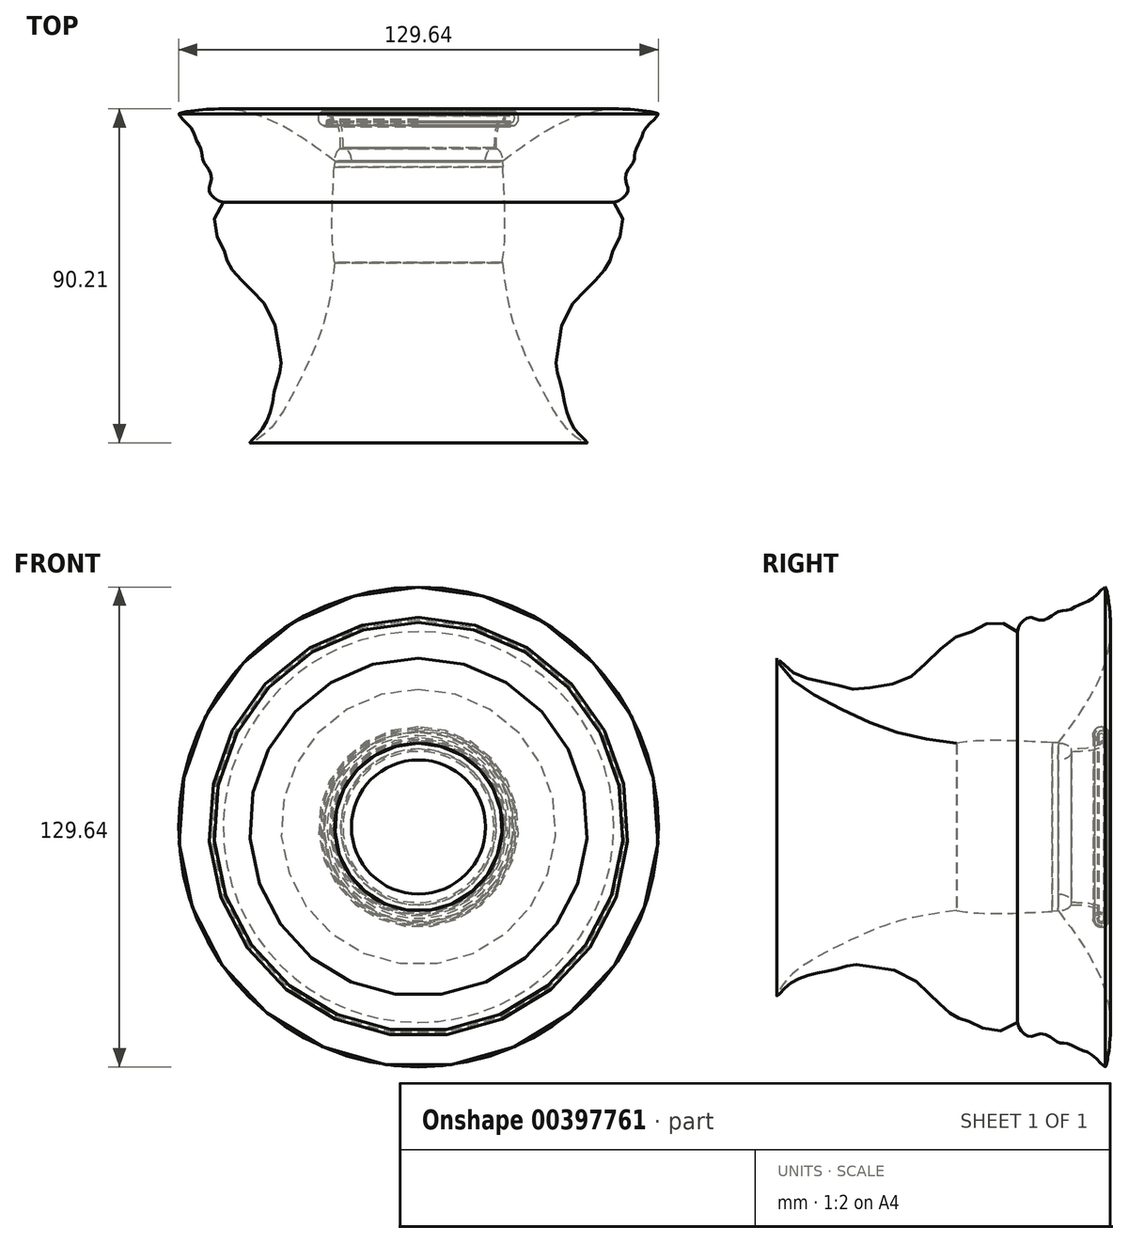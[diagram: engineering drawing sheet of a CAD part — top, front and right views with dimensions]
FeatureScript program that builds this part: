
annotation { "Feature Type Name" : "Feature", "Feature Type Description" : "" }
export const myFeature = defineFeature(function(context is Context, id is Id, definition is map)
    precondition{}
    {
        {
            var Q0;
            Q0=qCreatedBy(makeId("Top.planeOp"),FACE);
            var sketch = newSketch(context, id + "F0", { "sketchPlane" : qUnion([Q0])});
            skEllipticalArc(sketch, "E0", {});
            skEllipticalArc(sketch, "E1", {});
            skFitSpline(sketch, "E2", {"points": [v(2.3, 20.9) * mm, v(2.89, 0) * mm, v(1.74, -9.47) * mm], "startDerivative": vector(2.01, -38.53) * mm, "endDerivative": vector(-3.6, -21.18) * mm});
            skFitSpline(sketch, "E3", {"points": [v(-2.3, 20.9) * mm, v(-3.05, 0) * mm, v(-1.74, -9.47) * mm], "startDerivative": vector(-2.5, -38.54) * mm, "endDerivative": vector(4.14, -21.16) * mm});
            skEllipticalArc(sketch, "E4", {});
            skFitSpline(sketch, "E5", {"points": [v(-2.3, 20.9) * mm, v(0, 20.9) * mm, v(2.3, 20.9) * mm], "startDerivative": vector(4.7, -2.5) * mm, "endDerivative": vector(4.7, 2.5) * mm});
            skFitSpline(sketch, "E6", {"points": [v(-2.4, 19.25) * mm, v(0, 18.83) * mm, v(2.38, 19.24) * mm], "startDerivative": vector(4.9, -2.33) * mm, "endDerivative": vector(4.87, 2.3) * mm});
            skFitSpline(sketch, "E7", {"points": [v(2.3, 20.9) * mm, v(15.85, 30.1) * mm, v(32.92, 34.98) * mm, v(44.41, 33.58) * mm, v(36.58, 33.58) * mm, v(28.57, 33.06) * mm, v(16.1, 28.61) * mm, v(2.38, 19.24) * mm], "startDerivative": vector(81.12, 61.53) * mm, "endDerivative": vector(-77.6, -62.7) * mm});
            skFitSpline(sketch, "E8", {"points": [v(2.38, 19.24) * mm, v(12.47, 14.95) * mm, v(28.81, 10.34) * mm, v(32.38, 9.81) * mm, v(34.78, 10.9) * mm, v(36.24, 13.24) * mm, v(35.51, 15.87) * mm, v(36.39, 18.85) * mm, v(37.78, 20.9) * mm, v(38.21, 23.65) * mm, v(39.54, 26.37) * mm, v(41.1, 29.93) * mm, v(44.41, 33.58) * mm], "startDerivative": vector(70.32, -29.03) * mm, "endDerivative": vector(18.2, 40.24) * mm});
            skFitSpline(sketch, "E9", {"points": [v(2.22, -6.62) * mm, v(4.74, -21.24) * mm, v(9.72, -34.27) * mm, v(16.75, -47.59) * mm, v(22.16, -53.59) * mm, v(25.24, -55.2) * mm, v(22.5, -52.37) * mm, v(20.7, -49.53) * mm, v(19.34, -45.75) * mm, v(18.72, -42.23) * mm, v(17.47, -37.47) * mm, v(16.77, -34.04) * mm, v(17.42, -29.11) * mm, v(19.07, -20.9) * mm, v(22.35, -16.46) * mm, v(27.45, -11.2) * mm, v(31.06, -6.62) * mm, v(32.38, -2.5) * mm, v(34.51, 1.61) * mm, v(34.51, 6.21) * mm, v(32.38, 9.81) * mm], "startDerivative": vector(24.83, -191.18) * mm, "endDerivative": vector(-60.54, 80.48) * mm});
            skEllipse(sketch, "E10", {"center": v(28.24, 24.96) * mm, "majorRadius": 3.27 * mm, "minorRadius": 1.36 * mm, "majorAxis": v(0.84, 0.54)});
            skEllipse(sketch, "E11", {"center": v(28.24, 24.96) * mm, "majorRadius": 1.8 * mm, "minorRadius": 0.84 * mm, "majorAxis": v(0.82, 0.57)});
            skEllipse(sketch, "E12", {"center": v(24.15, 5.65) * mm, "majorRadius": 2.9 * mm, "minorRadius": 1.52 * mm, "majorAxis": v(0.82, -0.57)});
            skEllipse(sketch, "E13", {"center": v(24.15, 5.65) * mm, "majorRadius": 2.05 * mm, "minorRadius": 0.86 * mm, "majorAxis": v(0.76, -0.65)});
            skFitSpline(sketch, "E14", {"points": [v(2.22, -6.62) * mm, v(2.22, -6.56) * mm], "startDerivative": vector(0, 0.06) * mm, "endDerivative": vector(0, 0.06) * mm});
            skLineSegment(sketch, "E15", {"start": v(2.22, -6.56) * mm, "end": v(2.22, -6.55) * mm});
            skArc(sketch, "E16", {"start": v(3.2, 30.63) * mm, "mid": v(6.58, 31.93) * mm, "end": v(4.26, 34.7) * mm});
            skFitSpline(sketch, "E17", {"points": [v(0, 24.44) * mm, v(0.17, 27.52) * mm, v(0.46, 30.02) * mm, v(1.38, 32.67) * mm, v(2.86, 34.16) * mm, v(4.26, 34.7) * mm, v(5.9, 34.15) * mm, v(6.54, 33.17) * mm, v(6.42, 31.5) * mm, v(5.17, 30.4) * mm, v(3.2, 30.63) * mm, v(2.58, 32.37) * mm, v(3.43, 33.46) * mm, v(4.47, 33.63) * mm, v(5.32, 33.33) * mm, v(5.54, 32.83) * mm, v(5.46, 31.98) * mm, v(5, 31.43) * mm, v(4.06, 31.54) * mm, v(3.73, 32.07) * mm, v(4.64, 31.8) * mm, v(5.1, 32.7) * mm, v(4.5, 33.16) * mm, v(3.6, 33) * mm, v(3.02, 32.23) * mm, v(3.46, 31.08) * mm, v(5.02, 30.75) * mm, v(6.02, 31.63) * mm, v(6.13, 33.11) * mm, v(5.5, 33.9) * mm, v(4.27, 34.21) * mm, v(3.05, 33.74) * mm, v(1.87, 32.34) * mm, v(1.14, 29.93) * mm, v(0.72, 27.44) * mm, v(0.67, 24.28) * mm], "startDerivative": vector(3.76, 75.56) * mm, "endDerivative": vector(0.96, -77.04) * mm});
            skFitSpline(sketch, "E18", {"points": [v(2.38, 19.24) * mm, v(6.91, 21.58) * mm, v(16.42, 27.5) * mm, v(28.7, 31.98) * mm, v(36.58, 32.61) * mm, v(43.66, 33.11) * mm, v(36.58, 31.98) * mm, v(28.73, 31.35) * mm, v(16.53, 26.57) * mm, v(7.08, 21.11) * mm, v(2.38, 19.24) * mm]});
            skFitSpline(sketch, "E19", {"points": [v(3.89, 16) * mm, v(8, 13.7) * mm, v(12.47, 11.56) * mm, v(16.7, 10.04) * mm, v(24.01, 8.77) * mm, v(20.07, 8.11) * mm, v(20.15, 5.49) * mm, v(23.1, 2.28) * mm, v(26.97, 1.63) * mm, v(29.1, 2.7) * mm, v(27.05, 0.15) * mm, v(22.12, 1.05) * mm, v(18.5, 4.91) * mm, v(17.52, 7.43) * mm, v(12.47, 9.76) * mm, v(7.59, 12.3) * mm, v(3.89, 16) * mm]});
            skFitSpline(sketch, "E20", {"points": [v(5.46, 9.78) * mm, v(10.98, 6.1) * mm, v(15.51, 2.9) * mm, v(19.7, -3.33) * mm, v(18.04, -7.97) * mm, v(12.47, -7.2) * mm, v(12.47, -2.77) * mm, v(15.68, -3.9) * mm, v(13.83, -5.32) * mm, v(17.46, -5.96) * mm, v(17.35, -3.33) * mm, v(14.6, 0) * mm, v(9.86, 0) * mm, v(8.99, -8.85) * mm, v(10.9, -14.68) * mm, v(14.72, -14.4) * mm, v(16.47, -12.87) * mm, v(12.47, -19.72) * mm, v(12.04, -24.36) * mm, v(10.55, -27.84) * mm, v(8.92, -21.48) * mm, v(8.26, -16.46) * mm, v(7.13, -8.6) * mm, v(6.38, 0) * mm, v(6.08, 2.9) * mm, v(5.85, 7.32) * mm, v(5.46, 9.78) * mm]});
            skPoint(sketch, "E21.6.internal.snap0", {"position": v(27.52, 26.1) * mm});
            skFitSpline(sketch, "E21", {"points": [v(7.6, 19.77) * mm, v(15.95, 23.96) * mm, v(21.25, 26.36) * mm, v(24.34, 28.44) * mm, v(23.14, 24.47) * mm, v(23.41, 22.07) * mm, v(27.52, 21.38) * mm, v(29.13, 21.66) * mm, v(27.1, 19.54) * mm, v(23.04, 18.8) * mm, v(17.7, 18.9) * mm, v(12.3, 19.08) * mm, v(7.6, 19.77) * mm]});
            skFitSpline(sketch, "E22.MirrorCS", {"points": [v(-2.22, -6.62) * mm, v(-2.22, -6.56) * mm], "startDerivative": vector(0, 0.06) * mm, "endDerivative": vector(0, 0.06) * mm});
            skLineSegment(sketch, "E23.MirrorCS", {"start": v(-2.22, -6.56) * mm, "end": v(-2.22, -6.55) * mm});
            skEllipticalArc(sketch, "E24.MirrorCS", {});
            skEllipticalArc(sketch, "E25.MirrorCS", {});
            skFitSpline(sketch, "E26.MirrorCS", {"points": [v(2.3, 20.9) * mm, v(0, 20.9) * mm, v(-2.3, 20.9) * mm], "startDerivative": vector(-4.7, -2.5) * mm, "endDerivative": vector(-4.7, 2.5) * mm});
            skFitSpline(sketch, "E27.MirrorCS", {"points": [v(2.4, 19.25) * mm, v(0, 18.83) * mm, v(-2.38, 19.24) * mm], "startDerivative": vector(-4.9, -2.33) * mm, "endDerivative": vector(-4.87, 2.3) * mm});
            skEllipticalArc(sketch, "E28.MirrorCS", {});
            skLineSegment(sketch, "E29", {"start": v(-20.4, 52.86) * mm, "end": v(-20.4, -60.76) * mm});
            skPoint(sketch, "E30.orphan", {"position": v(0, 43.1) * mm});
            const initialGuessF0  = {"E0": [0, 0.02090463444890858, 0, -1, 0.0035310519394098046, 0.002297039903684678, 1.5707963267948966, 4.71238898038469], "E1": [0, -0.009469367382299913, 0, 1, 0.0035901373358472096, 0.001739675895624183, 1.5707963267948966, 4.71238898038469], "E4": [0.001387894892873516, 0.023718264862181527, 0.3162766123089874, -0.9486670145558718, 0.0018780809074936957, 0.0005518705882354958, 4.293777265012078, 0.42567047345905185], "E24.MirrorCS": [0, 0.02090463444890858, 0, -1, 0.0035310519394098046, 0.002297039903684678, 1.5707963267948966, 4.71238898038469], "E25.MirrorCS": [-0.001387894892873516, 0.023718264862181527, -0.3162766123089874, -0.9486670145558718, 0.0018780809074936957, 0.0005518705882354958, 5.8575148337205345, 1.9894080421675087], "E28.MirrorCS": [0, -0.009469367382299913, 0, 1, 0.0035901373358472096, 0.001739675895624183, 1.5707963267948966, 4.71238898038469]};
            skSetInitialGuess(sketch, initialGuessF0);
            skSolve(sketch);
        }
        {
            var Q0;
            Q0=makeQuery(id+"F0.imprint","IMPRINT",FACE,{"disambiguationData":[TD([[makeQuery(id+"F0.imprint","IMPRINT",EDGE,{"derivedFrom":sQuery(id+"F0.wireOp",EDGE,"E10")}),-1.0]])]});
            var Q1;
            Q1=makeQuery(id+"F0.imprint","IMPRINT",FACE,{"disambiguationData":[TD([[makeQuery(id+"F0.imprint","IMPRINT",EDGE,{"derivedFrom":sQuery(id+"F0.wireOp",EDGE,"E19")}),-1.0]])]});
            var Q2;
            Q2=makeQuery(id+"F0.imprint","IMPRINT",FACE,{"disambiguationData":[TD([[makeQuery(id+"F0.imprint","IMPRINT",EDGE,{"derivedFrom":sQuery(id+"F0.wireOp",EDGE,"E20")}),-1.0]])]});
            var Q3;
            Q3=makeQuery(id+"F0.imprint","IMPRINT",FACE,{"disambiguationData":[TD([[makeQuery(id+"F0.imprint","IMPRINT",EDGE,{"derivedFrom":sQuery(id+"F0.wireOp",EDGE,"E21")}),-1.0]])]});
            var Q4;
            {var subQ0=sQuery(id+"F0.wireOp",EDGE,"E9");Q4=makeQuery(id+"F0.imprint","IMPRINT",FACE,{"disambiguationData":[TD([[makeQuery(id+"F0.imprint","IMPRINT",EDGE,{"derivedFrom":subQ0}),1.0]])]});}
            var Q5;
            {var subQ1=sQuery(id+"F0.wireOp",EDGE,"E7");var subQ5=makeQuery(id+"F0.imprint","INTERSECT",VERTEX,{"derivedFrom":[subQ1,sQuery(id+"F0.wireOp",EDGE,"E8")]});Q5=makeQuery(id+"F0.imprint","IMPRINT",FACE,{"disambiguationData":[TD([[makeQuery(id+"F0.imprint","IMPRINT",EDGE,{"disambiguationData":[TD([[subQ5,-1.0]])],"derivedFrom":subQ1}),-1.0]])]});}
            var Q6;
            {var subQ0=sQuery(id+"F0.wireOp",EDGE,"E28.MirrorCS");Q6=makeQuery(id+"F0.imprint","IMPRINT",FACE,{"disambiguationData":[TD([[makeQuery(id+"F0.imprint","IMPRINT",EDGE,{"derivedFrom":subQ0}),1.0]])]});}
            var Q7;
            Q7=makeQuery(id+"F0.imprint","IMPRINT",FACE,{"disambiguationData":[TD([[makeQuery(id+"F0.imprint","IMPRINT",EDGE,{"derivedFrom":sQuery(id+"F0.wireOp",EDGE,"E10")}),1.0]])]});
            var Q8;
            Q8=makeQuery(id+"F0.imprint","IMPRINT",FACE,{"disambiguationData":[TD([[makeQuery(id+"F0.imprint","IMPRINT",EDGE,{"derivedFrom":sQuery(id+"F0.wireOp",EDGE,"E12")}),1.0]])]});
            var Q9;
            {var subQ0=sQuery(id+"F0.wireOp",EDGE,"E7");var subQ1=makeQuery(id+"F0.imprint","INTERSECT",VERTEX,{"derivedFrom":[subQ0,sQuery(id+"F0.wireOp",EDGE,"E27.MirrorCS")]});Q9=makeQuery(id+"F0.imprint","IMPRINT",FACE,{"disambiguationData":[TD([[makeQuery(id+"F0.imprint","IMPRINT",EDGE,{"disambiguationData":[TD([[subQ1,1.0]])],"derivedFrom":subQ0}),1.0]])]});}
            var Q10;
            {var subQ0=sQuery(id+"F0.wireOp",EDGE,"E17");var subQ1=sQuery(id+"F0.wireOp",EDGE,"E16");var subQ10=makeQuery(id+"F0.imprint","INTERSECT",VERTEX,{"disambiguationData":[OD(0.0)],"derivedFrom":[subQ1,subQ0]});Q10=makeQuery(id+"F0.imprint","IMPRINT",FACE,{"disambiguationData":[TD([[makeQuery(id+"F0.imprint","IMPRINT",EDGE,{"disambiguationData":[TD([[subQ10,-1.0]])],"derivedFrom":subQ1}),1.0]])]});}
            var Q11;
            Q11=makeQuery(id+"F0.imprint","IMPRINT",FACE,{"disambiguationData":[TD([[makeQuery(id+"F0.imprint","IMPRINT",EDGE,{"derivedFrom":sQuery(id+"F0.wireOp",EDGE,"E11")}),1.0]])]});
            var Q12;
            Q12=makeQuery(id+"F0.imprint","IMPRINT",FACE,{"disambiguationData":[TD([[makeQuery(id+"F0.imprint","IMPRINT",EDGE,{"derivedFrom":sQuery(id+"F0.wireOp",EDGE,"E13")}),1.0]])]});
            var Q13;
            {var subQ0=sQuery(id+"F0.wireOp",EDGE,"E4");Q13=makeQuery(id+"F0.imprint","IMPRINT",FACE,{"disambiguationData":[TD([[makeQuery(id+"F0.imprint","IMPRINT",EDGE,{"derivedFrom":subQ0}),1.0]])]});}
            var Q14;
            {var subQ0=sQuery(id+"F0.wireOp",EDGE,"E17");var subQ1=sQuery(id+"F0.wireOp",EDGE,"E16");var subQ2=makeQuery(id+"F0.imprint","INTERSECT",VERTEX,{"disambiguationData":[OD(3.0)],"derivedFrom":[subQ1,subQ0]});Q14=makeQuery(id+"F0.imprint","IMPRINT",FACE,{"disambiguationData":[TD([[makeQuery(id+"F0.imprint","IMPRINT",EDGE,{"disambiguationData":[TD([[subQ2,-1.0]])],"derivedFrom":subQ1}),-1.0]])]});}
            var Q15;
            {var subQ0=sQuery(id+"F0.wireOp",EDGE,"E17");var subQ1=sQuery(id+"F0.wireOp",EDGE,"E16");var subQ2=makeQuery(id+"F0.imprint","INTERSECT",VERTEX,{"disambiguationData":[OD(4.0)],"derivedFrom":[subQ1,subQ0]});Q15=makeQuery(id+"F0.imprint","IMPRINT",FACE,{"disambiguationData":[TD([[makeQuery(id+"F0.imprint","IMPRINT",EDGE,{"disambiguationData":[TD([[subQ2,-1.0]])],"derivedFrom":subQ1}),1.0]])]});}
            var Q16;
            {var subQ0=sQuery(id+"F0.wireOp",EDGE,"E17");var subQ1=sQuery(id+"F0.wireOp",EDGE,"E16");var subQ2=makeQuery(id+"F0.imprint","INTERSECT",VERTEX,{"disambiguationData":[OD(5.0)],"derivedFrom":[subQ1,subQ0]});Q16=makeQuery(id+"F0.imprint","IMPRINT",FACE,{"disambiguationData":[TD([[makeQuery(id+"F0.imprint","IMPRINT",EDGE,{"disambiguationData":[TD([[subQ2,-1.0]])],"derivedFrom":subQ1}),-1.0]])]});}
            var Q17;
            {var subQ0=sQuery(id+"F0.wireOp",EDGE,"E17");var subQ1=sQuery(id+"F0.wireOp",EDGE,"E16");var subQ2=makeQuery(id+"F0.imprint","INTERSECT",VERTEX,{"disambiguationData":[OD(0.0)],"derivedFrom":[subQ1,subQ0]});Q17=makeQuery(id+"F0.imprint","IMPRINT",FACE,{"disambiguationData":[TD([[makeQuery(id+"F0.imprint","IMPRINT",EDGE,{"disambiguationData":[TD([[subQ2,-1.0]])],"derivedFrom":subQ1}),-1.0]])]});}
            var Q18;
            {var subQ0=sQuery(id+"F0.wireOp",EDGE,"E17");var subQ1=sQuery(id+"F0.wireOp",EDGE,"E16");var subQ2=makeQuery(id+"F0.imprint","INTERSECT",VERTEX,{"disambiguationData":[OD(2.0)],"derivedFrom":[subQ1,subQ0]});Q18=makeQuery(id+"F0.imprint","IMPRINT",FACE,{"disambiguationData":[TD([[makeQuery(id+"F0.imprint","IMPRINT",EDGE,{"disambiguationData":[TD([[subQ2,-1.0]])],"derivedFrom":subQ1}),1.0]])]});}
            var Q19;
            {var subQ0=sQuery(id+"F0.wireOp",EDGE,"E17");var subQ1=sQuery(id+"F0.wireOp",EDGE,"E16");var subQ2=makeQuery(id+"F0.imprint","INTERSECT",VERTEX,{"disambiguationData":[OD(1.0)],"derivedFrom":[subQ1,subQ0]});Q19=makeQuery(id+"F0.imprint","IMPRINT",FACE,{"disambiguationData":[TD([[makeQuery(id+"F0.imprint","IMPRINT",EDGE,{"disambiguationData":[TD([[subQ2,1.0]])],"derivedFrom":subQ1}),1.0]])]});}
            var Q20;
            {var subQ5=sQuery(id+"F0.wireOp",EDGE,"E4");Q20=makeQuery(id+"F0.imprint","IMPRINT",FACE,{"disambiguationData":[TD([[makeQuery(id+"F0.imprint","IMPRINT",EDGE,{"derivedFrom":subQ5}),-1.0]])]});}
            var Q21;
            {var subQ0=sQuery(id+"F0.wireOp",EDGE,"E25.MirrorCS");Q21=makeQuery(id+"F0.imprint","IMPRINT",FACE,{"disambiguationData":[TD([[makeQuery(id+"F0.imprint","IMPRINT",EDGE,{"derivedFrom":subQ0}),1.0]])]});}
            var Q22;
            {var subQ0=sQuery(id+"F0.wireOp",EDGE,"E26.MirrorCS");Q22=makeQuery(id+"F0.imprint","IMPRINT",FACE,{"disambiguationData":[TD([[makeQuery(id+"F0.imprint","IMPRINT",EDGE,{"derivedFrom":subQ0}),1.0]])]});}
            var Q23;
            {var subQ0=sQuery(id+"F0.wireOp",EDGE,"E27.MirrorCS");var subQ1=sQuery(id+"F0.wireOp",EDGE,"E2");var subQ2=makeQuery(id+"F0.imprint","INTERSECT",VERTEX,{"derivedFrom":[subQ1,subQ0]});Q23=makeQuery(id+"F0.imprint","IMPRINT",FACE,{"disambiguationData":[TD([[makeQuery(id+"F0.imprint","IMPRINT",EDGE,{"disambiguationData":[TD([[subQ2,-1.0]])],"derivedFrom":subQ1}),-1.0]])]});}
            var Q24;
            {var subQ0=sQuery(id+"F0.wireOp",EDGE,"E27.MirrorCS");var subQ1=sQuery(id+"F0.wireOp",EDGE,"E7");var subQ2=makeQuery(id+"F0.imprint","INTERSECT",VERTEX,{"derivedFrom":[subQ1,subQ0]});Q24=makeQuery(id+"F0.imprint","IMPRINT",FACE,{"disambiguationData":[TD([[makeQuery(id+"F0.imprint","IMPRINT",EDGE,{"disambiguationData":[TD([[subQ2,1.0]])],"derivedFrom":subQ1}),-1.0]])]});}
            var Q25;
            {var subQ0=sQuery(id+"F0.wireOp",EDGE,"E18");var subQ1=sQuery(id+"F0.wireOp",EDGE,"E2");var subQ3=makeQuery(id+"F0.imprint","INTERSECT",VERTEX,{"derivedFrom":[subQ1,subQ0]});Q25=makeQuery(id+"F0.imprint","IMPRINT",FACE,{"disambiguationData":[TD([[makeQuery(id+"F0.imprint","IMPRINT",EDGE,{"disambiguationData":[TD([[subQ3,-1.0]])],"derivedFrom":subQ1}),-1.0]])]});}
            var Q26;
            {var subQ0=sQuery(id+"F0.wireOp",EDGE,"E18");var subQ1=sQuery(id+"F0.wireOp",EDGE,"E8");var subQ3=makeQuery(id+"F0.imprint","INTERSECT",VERTEX,{"derivedFrom":[subQ1,subQ0]});Q26=makeQuery(id+"F0.imprint","IMPRINT",FACE,{"disambiguationData":[TD([[makeQuery(id+"F0.imprint","IMPRINT",EDGE,{"disambiguationData":[TD([[subQ3,1.0]])],"derivedFrom":subQ1}),-1.0]])]});}
            var Q27;
            {var subQ0=sQuery(id+"F0.wireOp",EDGE,"E18");var subQ2=sQuery(id+"F0.wireOp",EDGE,"E2");var subQ4=makeQuery(id+"F0.imprint","INTERSECT",VERTEX,{"derivedFrom":[subQ2,subQ0]});Q27=makeQuery(id+"F0.imprint","IMPRINT",FACE,{"disambiguationData":[TD([[makeQuery(id+"F0.imprint","IMPRINT",EDGE,{"disambiguationData":[TD([[subQ4,-1.0]])],"derivedFrom":subQ0}),-1.0]])]});}
            var Q28;
            {var subQ0=sQuery(id+"F0.wireOp",EDGE,"E27.MirrorCS");var subQ1=sQuery(id+"F0.wireOp",EDGE,"E2");var subQ2=makeQuery(id+"F0.imprint","INTERSECT",VERTEX,{"derivedFrom":[subQ1,subQ0]});Q28=makeQuery(id+"F0.imprint","IMPRINT",FACE,{"disambiguationData":[TD([[makeQuery(id+"F0.imprint","IMPRINT",EDGE,{"disambiguationData":[TD([[subQ2,-1.0]])],"derivedFrom":subQ1}),1.0]])]});}
            var Q29;
            Q29=sQuery(id+"F0.wireOp",EDGE,"E29");
            revolve(context, id + "F1", {"entities" : qUnion([Q0, Q1, Q2, Q3, Q4, Q5, Q6, Q7, Q8, Q9, Q10, Q11, Q12, Q13, Q14, Q15, Q16, Q17, Q18, Q19, Q20, Q21, Q22, Q23, Q24, Q25, Q26, Q27, Q28]), "axis" : qUnion([Q29]), "revolveType" : RevolveType.FULL});
        }
    });
